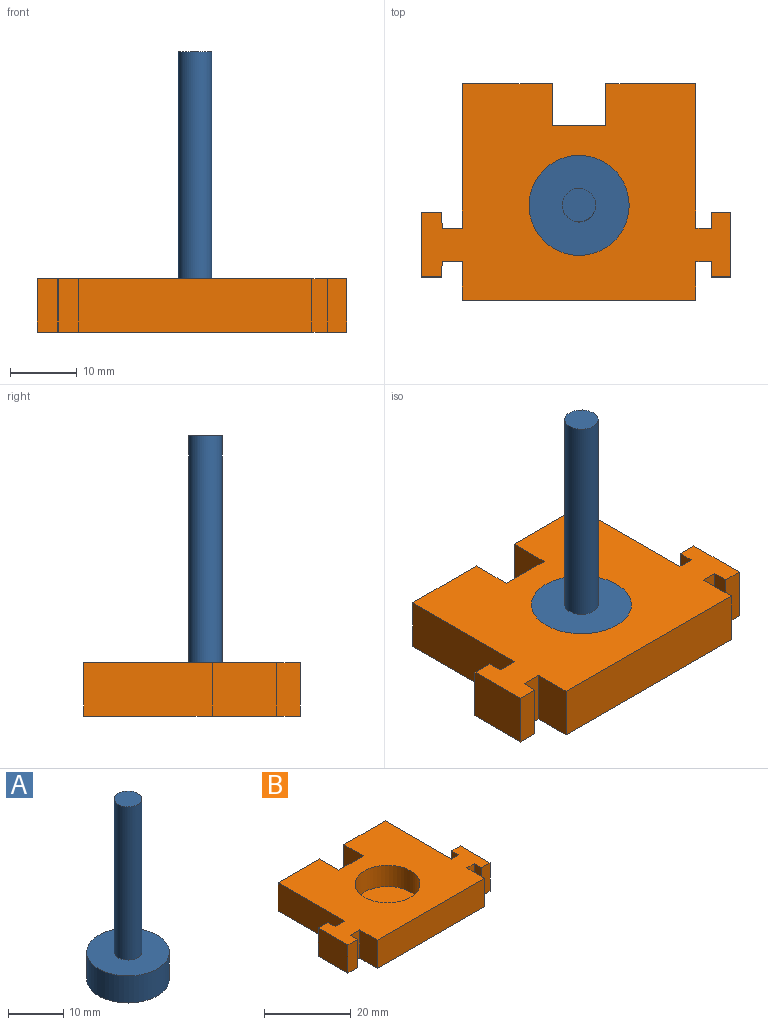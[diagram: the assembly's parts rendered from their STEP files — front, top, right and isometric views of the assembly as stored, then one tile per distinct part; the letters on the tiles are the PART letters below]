
ASSEMBLY  parts=2 mates=1
PART A: 5 faces, bbox 15x15x40 mm
  f0: cylinder r=7.5mm len=15mm, axis (0,0,-1), area 282.7mm2, adj f1,f2
  f1: plane 15x15mm, normal (0,0,1), area 157.1mm2, adj f0,f3
  f2: plane 15x15mm, normal (0,0,-1), area 176.7mm2, adj f0
  f3: cylinder r=2.5mm len=34mm, axis (0,0,-1), area 534.1mm2, adj f1,f4
  f4: plane 5x5mm, normal (0,0,1), area 19.6mm2, adj f3
PART B: 28 faces, bbox 46.4x32.5x8 mm
  f0: plane 13.49x8mm, normal (0,1,0), area 107.9mm2, adj f1,f24,f25,f26
  f1: plane 21.66x8mm, normal (-1,0,0), area 173.3mm2, adj f0,f2,f25,f26
  f2: plane 8x3.04mm, normal (0,1,0), area 24.4mm2, adj f1,f3,f25,f26
  f3: plane 8x2.3mm, normal (1,0.02,0), area 18.4mm2, adj f2,f4,f25,f26
  f4: plane 8x3.08mm, normal (0,1,0), area 24.7mm2, adj f3,f5,f25,f26
  f5: plane 9.63x8mm, normal (-1,0,0), area 77mm2, adj f4,f6,f25,f26
  f6: plane 8x3.08mm, normal (0,-1,0), area 24.7mm2, adj f5,f7,f25,f26
  f7: plane 8x2.33mm, normal (1,-0.02,0), area 18.6mm2, adj f6,f8,f25,f26
  f8: plane 8x3.04mm, normal (0,-1,0), area 24.4mm2, adj f7,f9,f25,f26
  f9: plane 8x5.84mm, normal (-1,0,0), area 46.7mm2, adj f8,f10,f25,f26
  f10: plane 35x8mm, normal (0,-1,0), area 280mm2, adj f9,f11,f25,f26
  f11: plane 8x5.84mm, normal (1,0,0), area 46.7mm2, adj f10,f12,f25,f26
  f12: plane 8x2.38mm, normal (0,-1,0), area 19mm2, adj f11,f13,f25,f26
  f13: plane 8x2.33mm, normal (-1,0,0), area 18.6mm2, adj f12,f14,f25,f26
  f14: plane 8x2.86mm, normal (0,-1,0), area 22.9mm2, adj f13,f15,f25,f26
  f15: plane 9.63x8mm, normal (1,0,0), area 77mm2, adj f14,f16,f25,f26
  f16: plane 8x2.86mm, normal (0,1,0), area 22.9mm2, adj f15,f17,f25,f26
  f17: plane 8x2.3mm, normal (-1,0,0), area 18.4mm2, adj f16,f18,f25,f26
  f18: plane 8x2.38mm, normal (0,1,0), area 19mm2, adj f17,f19,f25,f26
  f19: plane 21.66x8mm, normal (1,0,0), area 173.3mm2, adj f18,f20,f25,f26
  f20: plane 13.49x8mm, normal (0,1,0), area 107.9mm2, adj f19,f21,f25,f26
  f21: plane 8x6.35mm, normal (-1,0,0), area 50.8mm2, adj f20,f22,f25,f26
  f22: plane 8.02x8mm, normal (0,1,0), area 64.2mm2, adj f21,f24,f25,f26
  f23: cylinder r=7.5mm len=15mm, axis (0,0,-1), area 282.7mm2, adj f25,f27
  f24: plane 8x6.35mm, normal (1,0,0), area 50.8mm2, adj f0,f22,f25,f26
  f25: plane 46.4x32.5mm, normal (0,0,1), area 994.4mm2, adj f0,f1,f2,f3,f4,f5,f6,f7
  f26: plane 46.4x32.5mm, normal (0,0,-1), area 1171.2mm2, adj f0,f1,f2,f3,f4,f5,f6,f7
  f27: plane 15x15mm, normal (0,0,1), area 176.7mm2, adj f23
PLACE A t=(0,-35.76,2)mm
PLACE B at identity
MATE fastened A.f0 <-> B.f23  axis (0,0,-1) through (0,-35.76,2)mm
